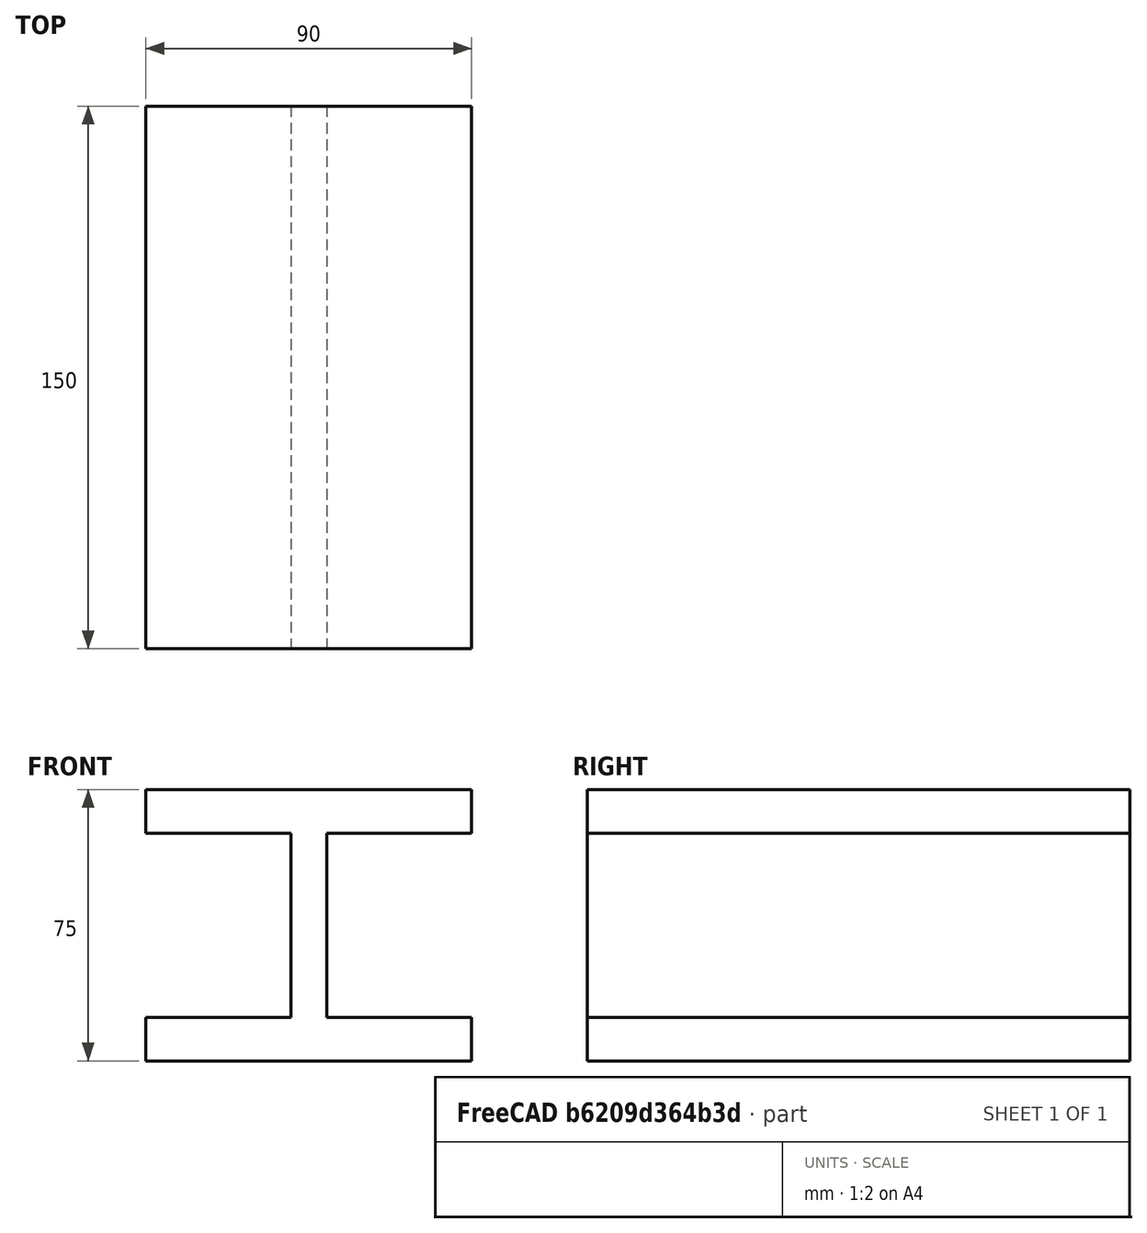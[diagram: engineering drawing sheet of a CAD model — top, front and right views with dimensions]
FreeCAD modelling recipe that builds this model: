
FCSTD DOCUMENT  (FreeCAD 0.21R33694 (Git))
Label: OJT1_T018_Tocho
License: All rights reserved
LicenseURL: https://en.wikipedia.org/wiki/All_rights_reserved
objects: Sketcher::SketchObject×1, PartDesign::Pad×1, PartDesign::Body×1
note: 4 computed .brp shape members not serialized (recipe doc carries the construction recipe); baked Part::Feature solids carry a one-line shape summary decoded from their .brp

FEATURE [Sketcher::SketchObject] Sketch
  FullyConstrained = false
  MapMode = 5
  Placement = pos=(0,0,0) rot=(1,0,0;1.5708rad)
  Support = -> [XZ_Plane]
  sketch-geometry (12):
    g0: LineSegment StartX=0 StartY=72.009 StartZ=0 EndX=90 EndY=72.009 EndZ=0
    g1: LineSegment StartX=90 StartY=72.009 StartZ=0 EndX=90 EndY=60.009 EndZ=0
    g2: LineSegment StartX=90 StartY=60.009 StartZ=0 EndX=50 EndY=60.009 EndZ=0
    g3: LineSegment StartX=50 StartY=60.009 StartZ=0 EndX=50 EndY=9.00902 EndZ=0
    g4: LineSegment StartX=50 StartY=9.00902 StartZ=0 EndX=90 EndY=9.00902 EndZ=0
    g5: LineSegment StartX=90 StartY=9.00902 StartZ=0 EndX=90 EndY=-2.99098 EndZ=0
    g6: LineSegment StartX=90 StartY=-2.99098 StartZ=0 EndX=0 EndY=-2.99098 EndZ=0
    g7: LineSegment StartX=0 StartY=-2.99098 StartZ=0 EndX=0 EndY=9.00902 EndZ=0
    g8: LineSegment StartX=0 StartY=9.00902 StartZ=0 EndX=40 EndY=9.00902 EndZ=0
    g9: LineSegment StartX=40 StartY=9.00902 StartZ=0 EndX=40 EndY=60.009 EndZ=0
    g10: LineSegment StartX=40 StartY=60.009 StartZ=0 EndX=0 EndY=60.009 EndZ=0
    g11: LineSegment StartX=0 StartY=60.009 StartZ=0 EndX=0 EndY=72.009 EndZ=0
  constraints (35):
    c: PointOnObject(g0,g-2)
    c: Horizontal(g0)
    c: Coincident(g0,g1)
    c: Coincident(g1,g2)
    c: Horizontal(g2)
    c: Coincident(g2,g3)
    c: Vertical(g3)
    c: Coincident(g3,g4)
    c: Horizontal(g4)
    c: Coincident(g4,g5)
    c: Coincident(g5,g6)
    c: Horizontal(g6)
    c: Coincident(g6,g7)
    c: Coincident(g7,g8)
    c: Coincident(g8,g9)
    c: Coincident(g9,g10)
    c: Horizontal(g10)
    c: Coincident(g10,g11)
    c: Coincident(g11,g0)
    c: Vertical(g11)
    c: Vertical(g9)
    c: Horizontal(g8)
    c: Vertical(g7)
    c: Vertical(g5)
    c: DistanceX(g0,g0) = 90
    c: DistanceX(g6,g6) = 90
    c: DistanceY(g11,g11) = 12
    c: DistanceY(g1,g1) = 12
    c: Vertical(g1)
    c: DistanceX(g10,g10) = 40
    c: DistanceX(g2,g2) = 40
    c: DistanceY(g7,g7) = 12
    c: DistanceX(g8,g8) = 40
    c: DistanceY(g3,g3) = 51
    c: DistanceY(g9,g9) = 51
FEATURE [PartDesign::Pad] Pad
  Direction = (0,-1,2e-16)
  Length = 150
  Length2 = 10
  Placement = pos=(0,0,0) rot=(1,0,0;1.5708rad)
  Profile = -> Sketch
  ReferenceAxis = -> Sketch [N_Axis]
  Type = 0
FEATURE [PartDesign::Body] Body
  Group = -> [Sketch,Pad]
  Origin = -> Origin
  Tip = -> Pad
